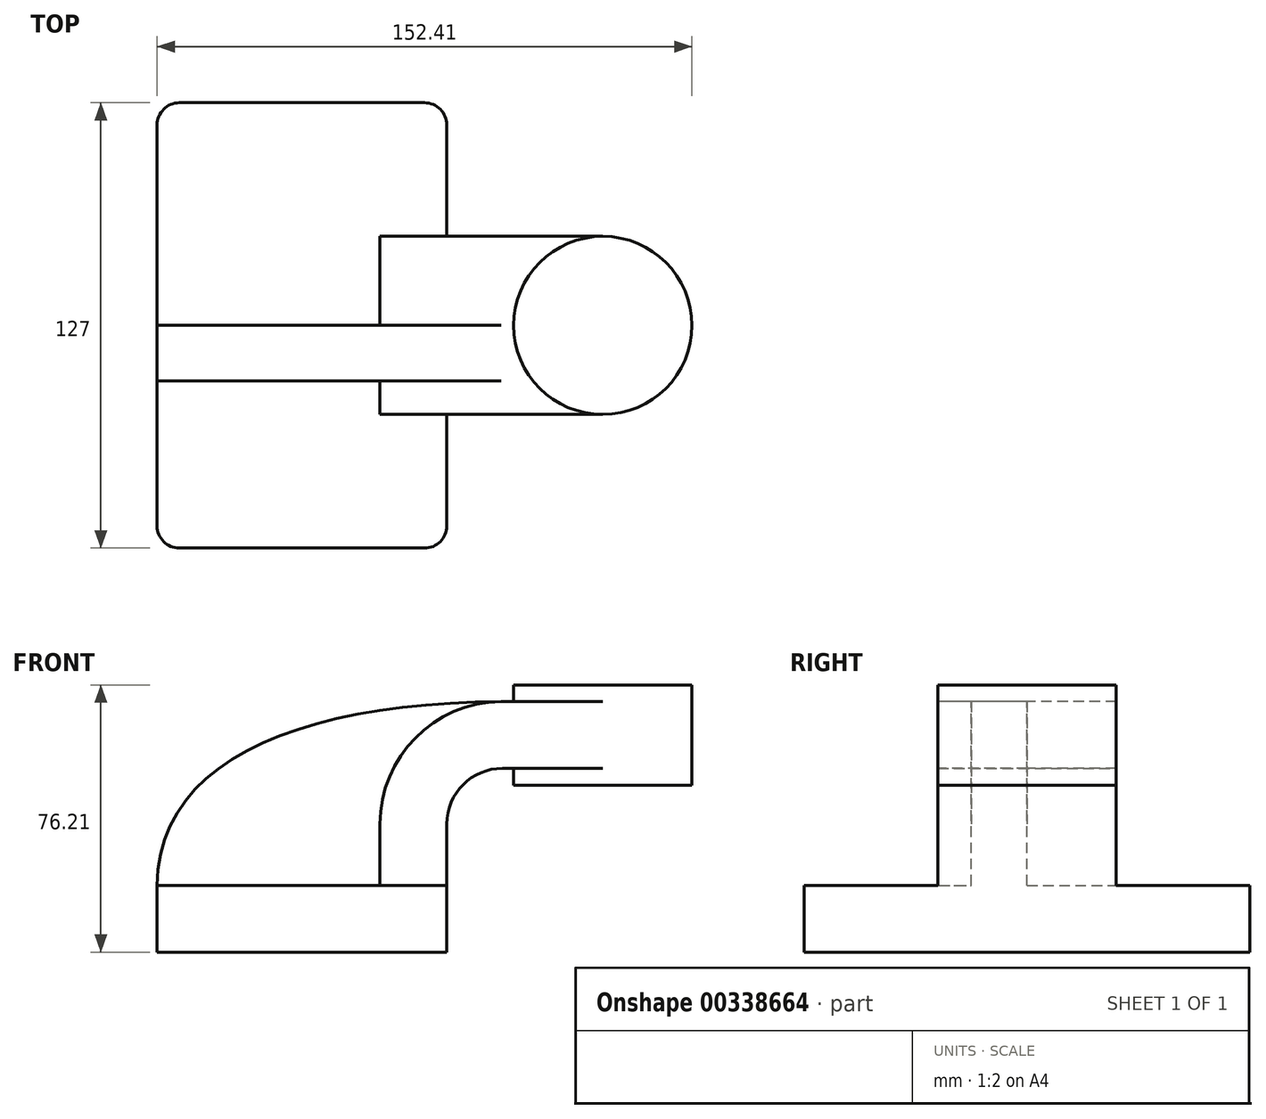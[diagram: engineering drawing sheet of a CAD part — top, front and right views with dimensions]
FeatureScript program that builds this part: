
annotation { "Feature Type Name" : "Feature", "Feature Type Description" : "" }
export const myFeature = defineFeature(function(context is Context, id is Id, definition is map)
    precondition{}
    {
        {
            var Q0;
            Q0=qCreatedBy(makeId("Front.planeOp"),FACE);
            var sketch = newSketch(context, id + "F0", { "sketchPlane" : qUnion([Q0])});
            skLineSegment(sketch, "E0.bottom", {"start": v(-41.28, 9.52) * mm, "end": v(41.27, 9.53) * mm});
            skLineSegment(sketch, "E0.top", {"start": v(-41.28, -9.53) * mm, "end": v(41.28, -9.53) * mm});
            skLineSegment(sketch, "E0.left", {"start": v(-41.28, 9.52) * mm, "end": v(-41.27, -9.53) * mm});
            skLineSegment(sketch, "E0.right", {"start": v(41.28, 9.53) * mm, "end": v(41.28, -9.52) * mm});
            skPoint(sketch, "E0.middle", {"position": v(0, 0) * mm});
            skLineSegment(sketch, "E1.bottom", {"start": v(60.33, 66.67) * mm, "end": v(111.12, 66.67) * mm});
            skLineSegment(sketch, "E1.top", {"start": v(60.33, 38.1) * mm, "end": v(111.12, 38.1) * mm});
            skLineSegment(sketch, "E1.left", {"start": v(60.33, 66.67) * mm, "end": v(60.33, 38.1) * mm});
            skLineSegment(sketch, "E1.right", {"start": v(111.12, 66.67) * mm, "end": v(111.13, 38.1) * mm});
            skPoint(sketch, "E1.middle", {"position": v(85.73, 52.39) * mm});
            skLineSegment(sketch, "E2", {"start": v(41.27, 9.53) * mm, "end": v(41.27, 27) * mm});
            skArc(sketch, "E3", {"start": v(41.27, 27) * mm, "mid": v(45.92, 38.23) * mm, "end": v(57.15, 42.88) * mm});
            skLineSegment(sketch, "E4", {"start": v(57.15, 42.88) * mm, "end": v(85.73, 42.88) * mm});
            skLineSegment(sketch, "E5.0", {"start": v(57.15, 61.93) * mm, "end": v(85.73, 61.93) * mm});
            skArc(sketch, "E5.1", {"start": v(22.23, 27) * mm, "mid": v(32.45, 51.7) * mm, "end": v(57.15, 61.93) * mm});
            skLineSegment(sketch, "E5.2", {"start": v(22.22, 9.53) * mm, "end": v(22.22, 27) * mm});
            skLineSegment(sketch, "E6", {"start": v(85.73, 38.1) * mm, "end": v(85.73, 66.67) * mm});
            skFitSpline(sketch, "E7", {"points": [v(-41.28, 9.52) * mm, v(57.15, 61.93) * mm], "startDerivative": vector(0.71, 107.4) * mm, "endDerivative": vector(171.45, 0.83) * mm});
            skSolve(sketch);
        }
        {
            var Q0;
            Q0=makeQuery(id+"F0.imprint","IMPRINT",FACE,{"disambiguationData":[TD([[makeQuery(id+"F0.imprint","IMPRINT",EDGE,{"derivedFrom":sQuery(id+"F0.wireOp",EDGE,"E0.top")}),1.0]])]});
            extrude(context, id + "F1", {"entities" : qUnion([Q0]), "endBound" : BoundingType.SYMMETRIC, "depth" : 127 * mm});
        }
        {
            var Q0;
            {var subQ1=sQuery(id+"F0.wireOp",EDGE,"E2");Q0=makeQuery(id+"F0.imprint","IMPRINT",FACE,{"disambiguationData":[TD([[makeQuery(id+"F0.imprint","IMPRINT",EDGE,{"derivedFrom":subQ1}),1.0]])]});}
            extrude(context, id + "F2", {"entities" : qUnion([Q0]), "operationType" : NewBodyOperationType.ADD, "endBound" : BoundingType.SYMMETRIC, "depth" : 50.8 * mm});
        }
        {
            var Q0;
            {var subQ3=sQuery(id+"F0.wireOp",EDGE,"E5.2");Q0=makeQuery(id+"F0.imprint","IMPRINT",FACE,{"disambiguationData":[TD([[makeQuery(id+"F0.imprint","IMPRINT",EDGE,{"derivedFrom":subQ3}),1.0]])]});}
            extrude(context, id + "F3", {"entities" : qUnion([Q0]), "operationType" : NewBodyOperationType.ADD, "depth" : 15.88 * mm});
        }
        {
            var Q0;
            {var subQ0=sQuery(id+"F0.wireOp",EDGE,"E5.0");var subQ1=sQuery(id+"F0.wireOp",EDGE,"E1.left");var subQ2=makeQuery(id+"F0.imprint","INTERSECT",VERTEX,{"derivedFrom":[subQ1,subQ0]});Q0=makeQuery(id+"F0.imprint","IMPRINT",FACE,{"disambiguationData":[TD([[makeQuery(id+"F0.imprint","IMPRINT",EDGE,{"disambiguationData":[TD([[subQ2,-1.0]])],"derivedFrom":subQ1}),1.0]])]});}
            extrude(context, id + "F4", {"entities" : qUnion([Q0]), "operationType" : NewBodyOperationType.ADD, "endBound" : BoundingType.SYMMETRIC, "depth" : 50.8 * mm});
        }
        {
            var Q0;
            {var subQ4=sQuery(id+"F0.wireOp",EDGE,"E1.right");Q0=makeQuery(id+"F0.imprint","IMPRINT",FACE,{"disambiguationData":[TD([[makeQuery(id+"F0.imprint","IMPRINT",EDGE,{"derivedFrom":subQ4}),-1.0]])]});}
            var Q1;
            Q1=sQuery(id+"F0.wireOp",EDGE,"E6");
            revolve(context, id + "F5", {"operationType" : NewBodyOperationType.ADD, "entities" : qUnion([Q0]), "axis" : qUnion([Q1]), "revolveType" : RevolveType.FULL});
        }
        {
            var Q0;
            Q0=makeQuery(id+"F1.opExtrude","CAP_EDGE",EDGE,{"disambiguationData":[OSD([sQuery(id+"F0.wireOp",EDGE,"E0.right")])],"isStart":false});
            var Q1;
            Q1=makeQuery(id+"F1.opExtrude","CAP_EDGE",EDGE,{"disambiguationData":[OSD([sQuery(id+"F0.wireOp",EDGE,"E0.left")])],"isStart":false});
            var Q2;
            Q2=makeQuery(id+"F1.opExtrude","CAP_EDGE",EDGE,{"disambiguationData":[OSD([sQuery(id+"F0.wireOp",EDGE,"E0.right")])],"isStart":true});
            var Q3;
            Q3=makeQuery(id+"F1.opExtrude","CAP_EDGE",EDGE,{"disambiguationData":[OSD([sQuery(id+"F0.wireOp",EDGE,"E0.left")])],"isStart":true});
            fillet(context, id + "F6", {"entities" : qUnion([Q0, Q1, Q2, Q3]), "radius" : 6.35 * mm, "tangentPropagation" : true, "allowEdgeOverflow" : false});
        }
    });
